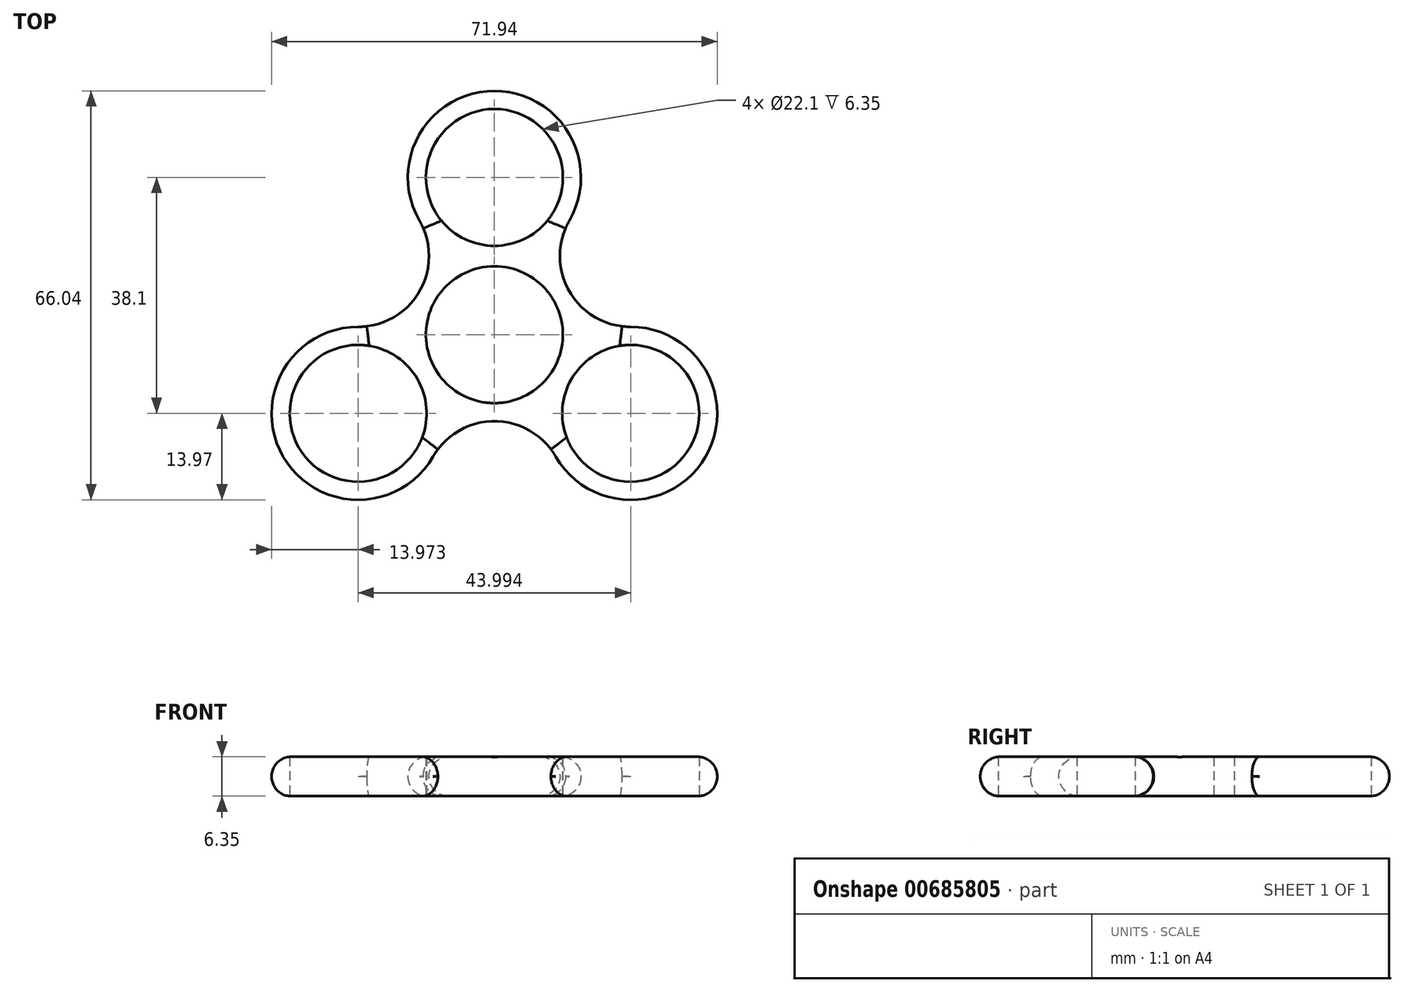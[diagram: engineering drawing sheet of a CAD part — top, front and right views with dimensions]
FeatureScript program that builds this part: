
annotation { "Feature Type Name" : "Feature", "Feature Type Description" : "" }
export const myFeature = defineFeature(function(context is Context, id is Id, definition is map)
    precondition{}
    {
        {
            var Q0;
            Q0=qCreatedBy(makeId("Top.planeOp"),FACE);
            var sketch = newSketch(context, id + "F0", { "sketchPlane" : qUnion([Q0])});
            skCircle(sketch, "E0", {"center": v(0, 0) * mm, "radius": 11.05 * mm});
            skCircle(sketch, "E1", {"center": v(0, 0) * mm, "radius": 13.97 * mm});
            skLineSegment(sketch, "E2", {"start": v(0, 0) * mm, "end": v(0, 25.4) * mm});
            skCircle(sketch, "E3", {"center": v(0, 25.4) * mm, "radius": 11.05 * mm});
            skCircle(sketch, "E4", {"center": v(0, 25.4) * mm, "radius": 13.97 * mm});
            skCircle(sketch, "E5.1.0", {"center": v(-22, -12.7) * mm, "radius": 11.05 * mm});
            skCircle(sketch, "E5.1.1", {"center": v(-22, -12.7) * mm, "radius": 13.97 * mm});
            skCircle(sketch, "E5.2.0", {"center": v(22, -12.7) * mm, "radius": 11.05 * mm});
            skCircle(sketch, "E5.2.1", {"center": v(22, -12.7) * mm, "radius": 13.97 * mm});
            skLineSegment(sketch, "E6", {"start": v(0, 0) * mm, "end": v(22, 12.7) * mm});
            skArc(sketch, "E7", {"start": v(12.1, 18.42) * mm, "mid": v(12.1, 6.99) * mm, "end": v(22, 1.27) * mm});
            skArc(sketch, "E8.1.0", {"start": v(-22, 1.27) * mm, "mid": v(-12.1, 6.98) * mm, "end": v(-12.1, 18.41) * mm});
            skArc(sketch, "E8.2.0", {"start": v(9.9, -19.69) * mm, "mid": v(0, -13.97) * mm, "end": v(-9.9, -19.69) * mm});
            skSolve(sketch);
        }
        {
            var Q0;
            Q0 = qSketchRegion(id + "F0", true);
            var Q1;
            {var subQ0=sQuery(id+"F0.wireOp",EDGE,"E5.1.1");var subQ1=sQuery(id+"F0.wireOp",EDGE,"E1");var subQ2=makeQuery(id+"F0.imprint","INTERSECT",VERTEX,{"disambiguationData":[OD(0.0)],"derivedFrom":[subQ1,subQ0]});Q1=makeQuery(id+"F0.imprint","IMPRINT",FACE,{"disambiguationData":[TD([[makeQuery(id+"F0.imprint","IMPRINT",EDGE,{"disambiguationData":[TD([[subQ2,-1.0]])],"derivedFrom":subQ1}),1.0]])]});}
            var Q2;
            {var subQ0=sQuery(id+"F0.wireOp",EDGE,"E5.2.1");var subQ1=sQuery(id+"F0.wireOp",EDGE,"E1");var subQ2=makeQuery(id+"F0.imprint","INTERSECT",VERTEX,{"disambiguationData":[OD(0.0)],"derivedFrom":[subQ1,subQ0]});Q2=makeQuery(id+"F0.imprint","IMPRINT",FACE,{"disambiguationData":[TD([[makeQuery(id+"F0.imprint","IMPRINT",EDGE,{"disambiguationData":[TD([[subQ2,-1.0]])],"derivedFrom":subQ1}),1.0]])]});}
            var Q3;
            {var subQ0=sQuery(id+"F0.wireOp",EDGE,"E2");var subQ1=sQuery(id+"F0.wireOp",EDGE,"E1");var subQ2=makeQuery(id+"F0.imprint","INTERSECT",VERTEX,{"derivedFrom":[subQ1,subQ0]});Q3=makeQuery(id+"F0.imprint","IMPRINT",FACE,{"disambiguationData":[TD([[makeQuery(id+"F0.imprint","IMPRINT",EDGE,{"disambiguationData":[TD([[subQ2,1.0]])],"derivedFrom":subQ1}),1.0]])]});}
            var Q4;
            {var subQ0=sQuery(id+"F0.wireOp",EDGE,"E2");var subQ1=sQuery(id+"F0.wireOp",EDGE,"E1");var subQ2=makeQuery(id+"F0.imprint","INTERSECT",VERTEX,{"derivedFrom":[subQ1,subQ0]});Q4=makeQuery(id+"F0.imprint","IMPRINT",FACE,{"disambiguationData":[TD([[makeQuery(id+"F0.imprint","IMPRINT",EDGE,{"disambiguationData":[TD([[subQ2,-1.0]])],"derivedFrom":subQ1}),1.0]])]});}
            extrude(context, id + "F1", {"entities" : qUnion([Q0, Q1, Q2, Q3, Q4]), "depth" : 6.35 * mm, "offsetDistance" : 25.4 * mm});
        }
        {
            var Q0;
            Q0=makeQuery(id+"F1.opExtrude","CAP_EDGE",EDGE,{"disambiguationData":[OSD([sQuery(id+"F0.wireOp",EDGE,"E5.1.1")])],"isStart":false});
            var Q1;
            Q1=makeQuery(id+"F1.opExtrude","CAP_EDGE",EDGE,{"disambiguationData":[OSD([sQuery(id+"F0.wireOp",EDGE,"E5.2.1")])],"isStart":true});
            fillet(context, id + "F2", {"entities" : qUnion([Q0, Q1]), "radius" : 3.17 * mm, "tangentPropagation" : true, "allowEdgeOverflow" : false});
        }
    });
